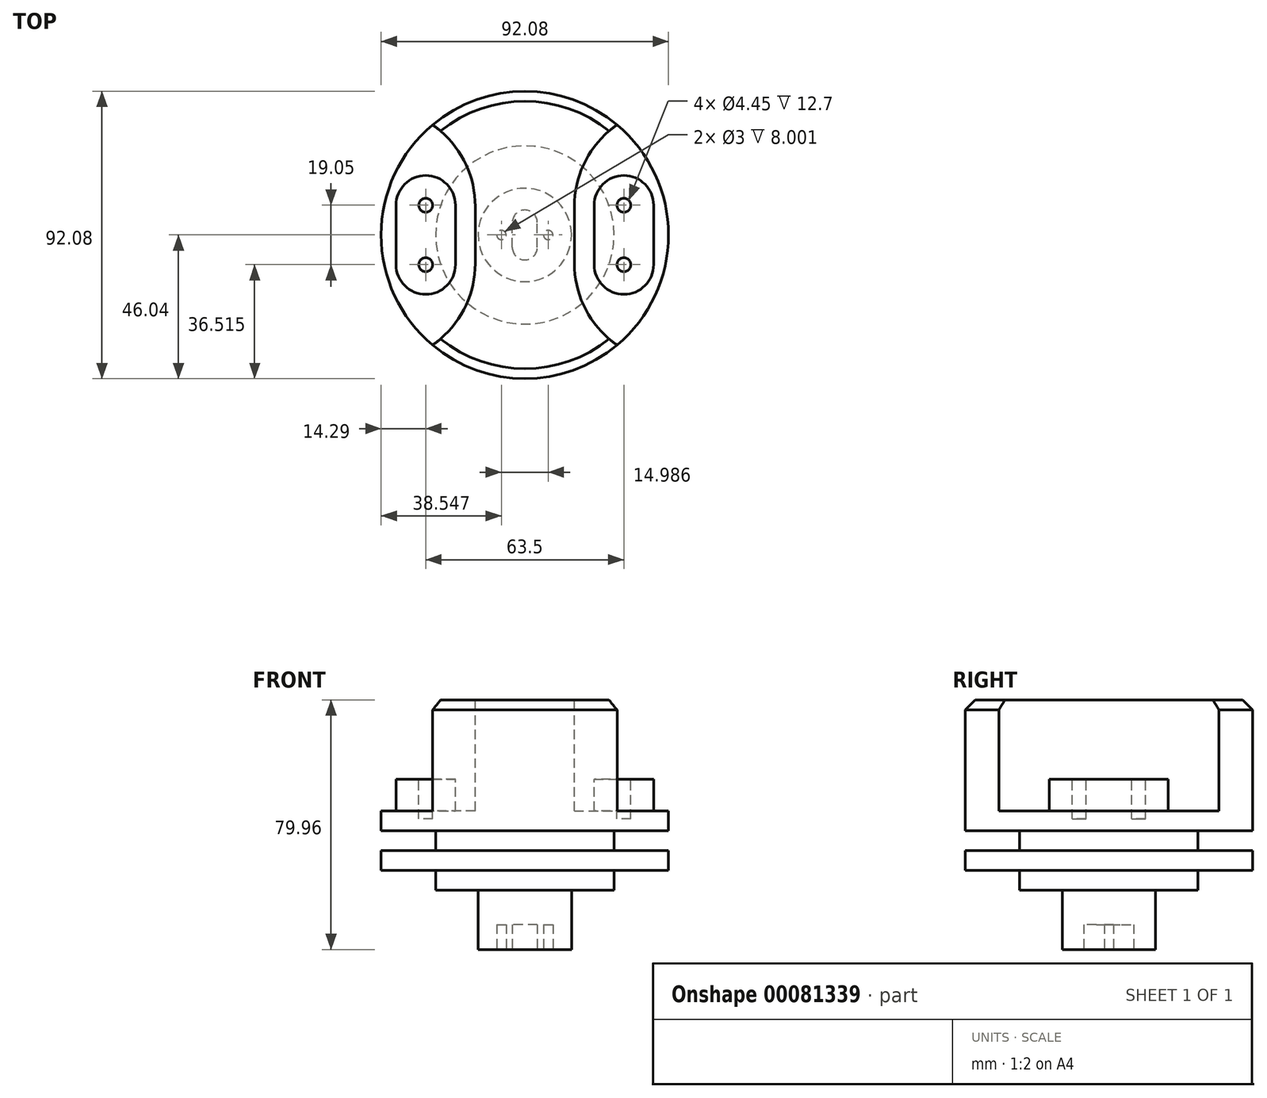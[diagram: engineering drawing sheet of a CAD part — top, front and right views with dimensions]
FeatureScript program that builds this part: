
annotation { "Feature Type Name" : "Feature", "Feature Type Description" : "" }
export const myFeature = defineFeature(function(context is Context, id is Id, definition is map)
    precondition{}
    {
        {
            var Q0;
            Q0=qCreatedBy(makeId("Front.planeOp"),FACE);
            var sketch = newSketch(context, id + "F0", { "sketchPlane" : qUnion([Q0])});
            skLineSegment(sketch, "E0", {"start": v(14.96, 0) * mm, "end": v(14.96, 19) * mm});
            skLineSegment(sketch, "E1", {"start": v(14.96, 19) * mm, "end": v(28.58, 19) * mm});
            skLineSegment(sketch, "E2", {"start": v(28.58, 19) * mm, "end": v(28.58, 25.35) * mm});
            skLineSegment(sketch, "E3", {"start": v(46.04, 25.35) * mm, "end": v(28.58, 25.35) * mm});
            skLineSegment(sketch, "E4", {"start": v(46.04, 25.35) * mm, "end": v(46.04, 31.7) * mm});
            skLineSegment(sketch, "E5", {"start": v(28.58, 31.7) * mm, "end": v(46.04, 31.7) * mm});
            skLineSegment(sketch, "E6", {"start": v(28.58, 31.7) * mm, "end": v(28.58, 38.05) * mm});
            skLineSegment(sketch, "E7", {"start": v(28.58, 38.05) * mm, "end": v(46.04, 38.05) * mm});
            skLineSegment(sketch, "E8", {"start": v(46.04, 38.05) * mm, "end": v(46.04, 44.4) * mm});
            skLineSegment(sketch, "E9", {"start": v(46.04, 79.96) * mm, "end": v(0, 79.96) * mm});
            skLineSegment(sketch, "E10", {"start": v(0, 79.96) * mm, "end": v(0, 0) * mm});
            skLineSegment(sketch, "E11", {"start": v(0, 0) * mm, "end": v(14.96, 0) * mm});
            skLineSegment(sketch, "E12", {"start": v(46.04, 44.4) * mm, "end": v(46.04, 44.4) * mm});
            skLineSegment(sketch, "E13", {"start": v(46.04, 44.4) * mm, "end": v(46.04, 50.75) * mm});
            skLineSegment(sketch, "E14", {"start": v(46.04, 50.75) * mm, "end": v(46.04, 50.75) * mm});
            skLineSegment(sketch, "E15.trimOffspring", {"start": v(46.04, 50.75) * mm, "end": v(46.04, 79.96) * mm});
            skSolve(sketch);
        }
        {
            var Q0;
            Q0=makeQuery(id+"F0.imprint","IMPRINT",FACE,{"disambiguationData":[TD([[makeQuery(id+"F0.imprint","IMPRINT",EDGE,{"derivedFrom":sQuery(id+"F0.wireOp",EDGE,"E0")}),1.0]])]});
            var Q1;
            Q1=sQuery(id+"F0.wireOp",EDGE,"E10");
            revolve(context, id + "F1", {"surfaceOperationType" : NewSurfaceOperationType.NEW, "entities" : qUnion([Q0]), "axis" : qUnion([Q1]), "revolveType" : RevolveType.FULL});
        }
        {
            var Q0;
            Q0=makeQuery(id+"F1.opRevolve","SWEPT_FACE",FACE,{"disambiguationData":[OSD([sQuery(id+"F0.wireOp",EDGE,"E9")])]});
            var sketch = newSketch(context, id + "F2", { "sketchPlane" : qUnion([Q0])});
            skLineSegment(sketch, "E16", {"start": v(15.88, -9.17) * mm, "end": v(15.88, 9.17) * mm});
            skLineSegment(sketch, "E17", {"start": v(-6.35, 53.72) * mm, "end": v(-6.35, -53.72) * mm});
            skLineSegment(sketch, "E18", {"start": v(-6.35, -53.72) * mm, "end": v(6.35, -53.72) * mm});
            skLineSegment(sketch, "E19", {"start": v(6.35, -53.72) * mm, "end": v(6.35, 53.72) * mm});
            skLineSegment(sketch, "E20", {"start": v(6.35, 53.72) * mm, "end": v(-6.35, 53.72) * mm});
            skLineSegment(sketch, "E21", {"start": v(0, 0) * mm, "end": v(0, -53.72) * mm, "construction": true});
            skLineSegment(sketch, "E22", {"start": v(0, 0) * mm, "end": v(76.66, -44.26) * mm, "construction": true});
            skLineSegment(sketch, "E23.0", {"start": v(11.34, -17.54) * mm, "end": v(71.9, -52.5) * mm, "construction": true});
            skLineSegment(sketch, "E24.0", {"start": v(10.9, -24.62) * mm, "end": v(68.72, -58) * mm});
            skArc(sketch, "E25", {"start": v(15.88, -9.17) * mm, "mid": v(20.13, -25.04) * mm, "end": v(31.75, -36.66) * mm});
            skCircle(sketch, "E26", {"center": v(31.75, 9.52) * mm, "radius": 2.22 * mm});
            skCircle(sketch, "E27", {"center": v(31.75, -9.53) * mm, "radius": 2.22 * mm});
            skCircle(sketch, "E28", {"center": v(-31.75, 9.52) * mm, "radius": 2.22 * mm});
            skCircle(sketch, "E29", {"center": v(-31.75, -9.53) * mm, "radius": 2.22 * mm});
            skLineSegment(sketch, "E30", {"start": v(0, 0) * mm, "end": v(-57.08, 0) * mm, "construction": true});
            skPoint(sketch, "E30.endSnap0", {"position": v(-6.35, 0) * mm});
            skArc(sketch, "E31.MirrorCS", {"start": v(15.88, 9.17) * mm, "mid": v(20.13, 25.04) * mm, "end": v(31.75, 36.66) * mm});
            skArc(sketch, "E32.MirrorCS", {"start": v(-15.88, 9.17) * mm, "mid": v(-20.13, 25.04) * mm, "end": v(-31.75, 36.66) * mm});
            skArc(sketch, "E33.MirrorCS", {"start": v(-15.88, -9.17) * mm, "mid": v(-20.13, -25.04) * mm, "end": v(-31.75, -36.66) * mm});
            skLineSegment(sketch, "E34.MirrorCS", {"start": v(-15.88, -9.17) * mm, "end": v(-15.88, 9.17) * mm});
            skArc(sketch, "E35", {"start": v(41.27, 9.53) * mm, "mid": v(31.75, 19.05) * mm, "end": v(22.23, 9.53) * mm});
            skArc(sketch, "E36.MirrorCS", {"start": v(41.28, -9.52) * mm, "mid": v(31.75, -19.05) * mm, "end": v(22.23, -9.52) * mm});
            skLineSegment(sketch, "E37", {"start": v(22.23, 9.53) * mm, "end": v(22.23, -9.52) * mm});
            skLineSegment(sketch, "E38", {"start": v(41.28, 9.53) * mm, "end": v(41.28, -9.52) * mm});
            skArc(sketch, "E39.MirrorCS", {"start": v(-41.28, -9.52) * mm, "mid": v(-31.75, -19.05) * mm, "end": v(-22.23, -9.52) * mm});
            skLineSegment(sketch, "E40.MirrorCS", {"start": v(-22.23, 9.53) * mm, "end": v(-22.23, -9.52) * mm});
            skArc(sketch, "E41.MirrorCS", {"start": v(-41.27, 9.53) * mm, "mid": v(-31.75, 19.05) * mm, "end": v(-22.23, 9.53) * mm});
            skLineSegment(sketch, "E42.MirrorCS", {"start": v(-41.28, 9.53) * mm, "end": v(-41.28, -9.52) * mm});
            skSolve(sketch);
        }
        {
            var Q0;
            Q0=makeQuery(id+"F2.imprint","IMPRINT",FACE,{"disambiguationData":[TD([[makeQuery(id+"F2.imprint","IMPRINT",EDGE,{"derivedFrom":sQuery(id+"F2.wireOp",EDGE,"E26")}),-1.0]])]});
            var Q1;
            Q1=makeQuery(id+"F2.imprint","IMPRINT",FACE,{"disambiguationData":[TD([[makeQuery(id+"F2.imprint","IMPRINT",EDGE,{"derivedFrom":sQuery(id+"F2.wireOp",EDGE,"E28")}),-1.0]])]});
            extrude(context, id + "F3", {"entities" : qUnion([Q0, Q1]), "operationType" : NewBodyOperationType.REMOVE, "oppositeDirection" : true, "depth" : 25.4 * mm, "offsetDistance" : 25.4 * mm});
        }
        {
            var Q0;
            {var subQ1=sQuery(id+"F2.wireOp",EDGE,"E16");Q0=makeQuery(id+"F2.imprint","IMPRINT",FACE,{"disambiguationData":[TD([[makeQuery(id+"F2.imprint","IMPRINT",EDGE,{"derivedFrom":subQ1}),-1.0]])]});}
            var Q1;
            {var subQ0=sQuery(id+"F2.wireOp",EDGE,"E34.MirrorCS");Q1=makeQuery(id+"F2.imprint","IMPRINT",FACE,{"disambiguationData":[TD([[makeQuery(id+"F2.imprint","IMPRINT",EDGE,{"derivedFrom":subQ0}),1.0]])]});}
            extrude(context, id + "F4", {"entities" : qUnion([Q0, Q1]), "operationType" : NewBodyOperationType.REMOVE, "oppositeDirection" : true, "depth" : 35.56 * mm, "offsetDistance" : 25.4 * mm});
        }
        {
            var Q0;
            Q0=makeQuery(id+"F2.imprint","IMPRINT",FACE,{"disambiguationData":[TD([[makeQuery(id+"F2.imprint","IMPRINT",EDGE,{"derivedFrom":sQuery(id+"F2.wireOp",EDGE,"E28")}),1.0]])]});
            var Q1;
            Q1=makeQuery(id+"F2.imprint","IMPRINT",FACE,{"disambiguationData":[TD([[makeQuery(id+"F2.imprint","IMPRINT",EDGE,{"derivedFrom":sQuery(id+"F2.wireOp",EDGE,"E29")}),1.0]])]});
            var Q2;
            Q2=makeQuery(id+"F2.imprint","IMPRINT",FACE,{"disambiguationData":[TD([[makeQuery(id+"F2.imprint","IMPRINT",EDGE,{"derivedFrom":sQuery(id+"F2.wireOp",EDGE,"E26")}),1.0]])]});
            var Q3;
            Q3=makeQuery(id+"F2.imprint","IMPRINT",FACE,{"disambiguationData":[TD([[makeQuery(id+"F2.imprint","IMPRINT",EDGE,{"derivedFrom":sQuery(id+"F2.wireOp",EDGE,"E27")}),1.0]])]});
            extrude(context, id + "F5", {"entities" : qUnion([Q0, Q1, Q2, Q3]), "operationType" : NewBodyOperationType.REMOVE, "oppositeDirection" : true, "depth" : 38.1 * mm, "offsetDistance" : 25.4 * mm});
        }
        {
            var Q0;
            {var subQ0=sQuery(id+"F0.wireOp",EDGE,"E15.trimOffspring");var subQ1=sQuery(id+"F0.wireOp",EDGE,"E9");Q0=makeQuery(id+"F4.boolean.opBoolean","SPLIT",EDGE,{"disambiguationData":[TD([makeQuery(id+"F4.opExtrude","SWEPT_FACE",FACE,{"disambiguationData":[OSD([sQuery(id+"F2.wireOp",EDGE,"E25")])]})])],"derivedFrom":makeQuery(id+"F1.opRevolve","SWEPT_EDGE",EDGE,{"disambiguationData":[OSD([subQ1,subQ0])]})});}
            var Q1;
            {var subQ0=sQuery(id+"F0.wireOp",EDGE,"E15.trimOffspring");var subQ1=sQuery(id+"F0.wireOp",EDGE,"E9");Q1=makeQuery(id+"F4.boolean.opBoolean","SPLIT",EDGE,{"disambiguationData":[TD([makeQuery(id+"F4.opExtrude","SWEPT_FACE",FACE,{"disambiguationData":[OSD([sQuery(id+"F2.wireOp",EDGE,"E31.MirrorCS")])]})])],"derivedFrom":makeQuery(id+"F1.opRevolve","SWEPT_EDGE",EDGE,{"disambiguationData":[OSD([subQ1,subQ0])]})});}
            chamfer(context, id + "F6", {"entities" : qUnion([Q0, Q1]), "width" : 3.17 * mm, "tangentPropagation" : true});
        }
        {
            var Q0;
            Q0=makeQuery(id+"F1.opRevolve","SWEPT_FACE",FACE,{"disambiguationData":[OSD([sQuery(id+"F0.wireOp",EDGE,"E11")])]});
            var sketch = newSketch(context, id + "F7", { "sketchPlane" : qUnion([Q0])});
            skLineSegment(sketch, "E43", {"start": v(4, 4) * mm, "end": v(4, -4) * mm});
            skLineSegment(sketch, "E44", {"start": v(-4, 4) * mm, "end": v(-4, -4) * mm});
            skArc(sketch, "E45", {"start": v(4, 4) * mm, "mid": v(0, 8) * mm, "end": v(-4, 4) * mm});
            skArc(sketch, "E46", {"start": v(-4, -4) * mm, "mid": v(0, -8) * mm, "end": v(4, -4) * mm});
            skCircle(sketch, "E47", {"center": v(-7.5, 0) * mm, "radius": 1.5 * mm});
            skCircle(sketch, "E48", {"center": v(7.5, 0) * mm, "radius": 1.5 * mm});
            skSolve(sketch);
        }
        {
            var Q0;
            Q0 = qSketchRegion(id + "F7", true);
            extrude(context, id + "F8", {"entities" : qUnion([Q0]), "operationType" : NewBodyOperationType.REMOVE, "oppositeDirection" : true, "depth" : 8 * mm, "offsetDistance" : 25.4 * mm});
        }
    });
